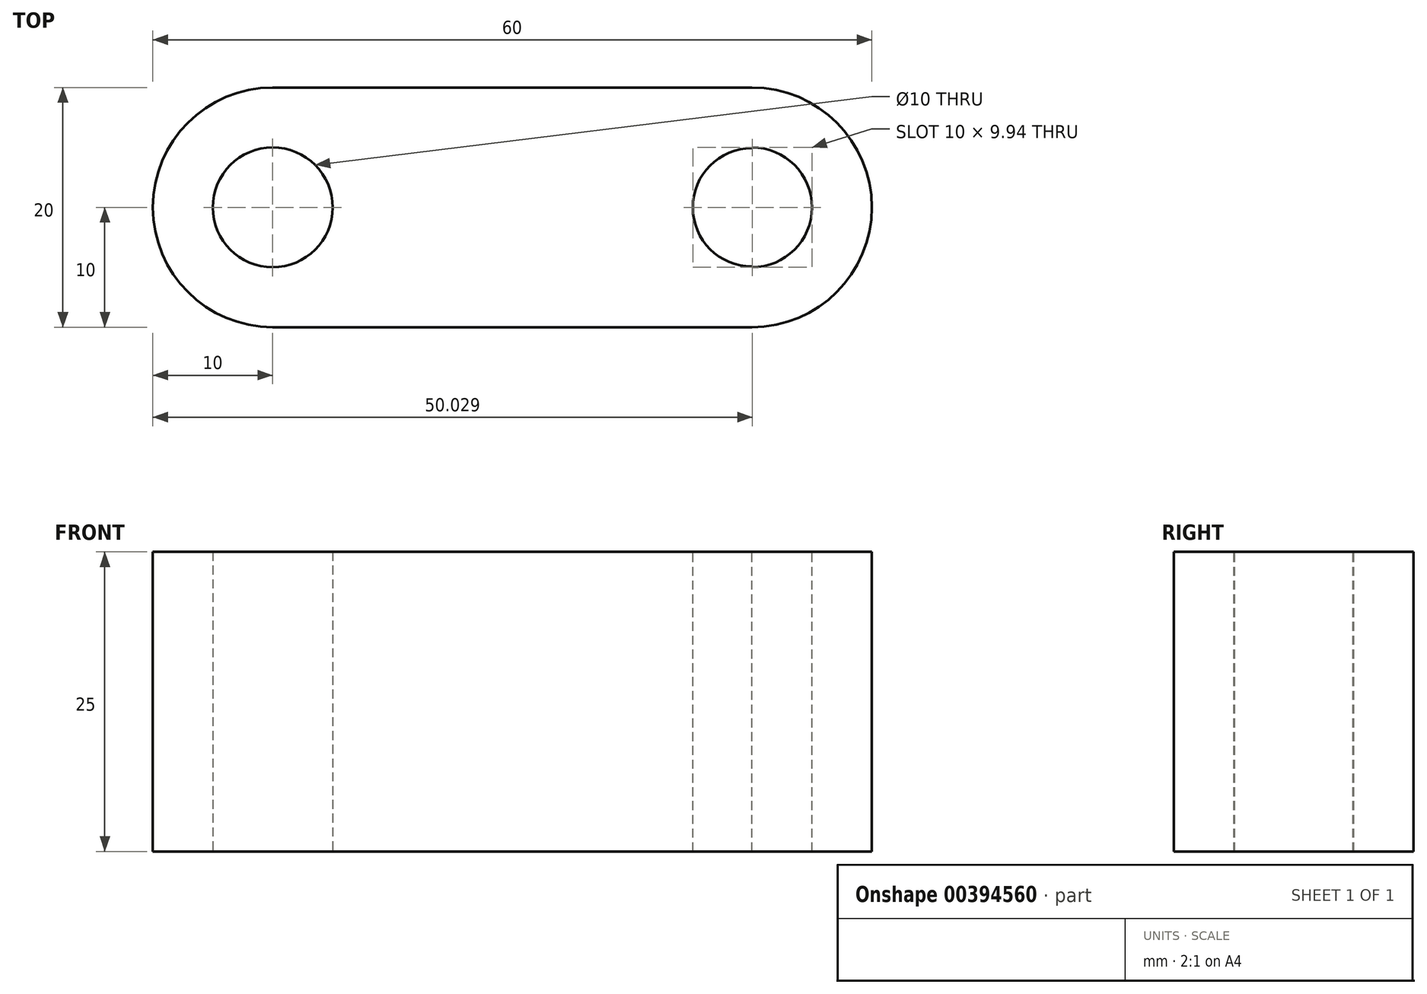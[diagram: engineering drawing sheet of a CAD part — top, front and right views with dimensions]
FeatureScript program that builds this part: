
annotation { "Feature Type Name" : "Feature", "Feature Type Description" : "" }
export const myFeature = defineFeature(function(context is Context, id is Id, definition is map)
    precondition{}
    {
        {
            var Q0;
            Q0=qCreatedBy(makeId("Top.planeOp"),FACE);
            var sketch = newSketch(context, id + "F0", { "sketchPlane" : qUnion([Q0])});
            skLineSegment(sketch, "E0.bottom", {"start": v(20, -10) * mm, "end": v(-20, -10) * mm});
            skLineSegment(sketch, "E0.top", {"start": v(20, 10) * mm, "end": v(-20, 10) * mm});
            skLineSegment(sketch, "E0.left", {"start": v(20, -10) * mm, "end": v(20, 10) * mm});
            skLineSegment(sketch, "E0.right", {"start": v(-20, -10) * mm, "end": v(-20, 10) * mm});
            skPoint(sketch, "E0.middle", {"position": v(0, 0) * mm});
            skCircle(sketch, "E1", {"center": v(-20, 0) * mm, "radius": 10 * mm});
            skCircle(sketch, "E2", {"center": v(-20, 0) * mm, "radius": 5 * mm});
            skSolve(sketch);
        }
        {
            var Q0;
            Q0 = qSketchRegion(id + "F0", true);
            extrude(context, id + "F1", {"entities" : qUnion([Q0]), "depth" : 25 * mm});
        }
        {
            var Q0;
            Q0=makeQuery(id+"F1.opExtrude","CAP_FACE",FACE,{"disambiguationData":[OSD([sQuery(id+"F0.wireOp",EDGE,"E0.bottom"),sQuery(id+"F0.wireOp",EDGE,"E0.top"),sQuery(id+"F0.wireOp",EDGE,"E0.left"),sQuery(id+"F0.wireOp",EDGE,"E1"),sQuery(id+"F0.wireOp",EDGE,"E2")])],"isStart":false});
            var sketch = newSketch(context, id + "F2", { "sketchPlane" : qUnion([Q0])});
            skCircle(sketch, "E3", {"center": v(20, 0) * mm, "radius": 10 * mm});
            skCircle(sketch, "E4", {"center": v(20, 0) * mm, "radius": 5 * mm});
            skSolve(sketch);
        }
        {
            var Q0;
            Q0 = qSketchRegion(id + "F2", true);
            extrude(context, id + "F3", {"entities" : qUnion([Q0]), "operationType" : NewBodyOperationType.ADD, "oppositeDirection" : true, "depth" : 25 * mm});
        }
        {
            var Q0;
            Q0=makeQuery(id+"F3.boolean.opBoolean","MERGE",FACE,{"derivedFrom":[makeQuery(id+"F1.opExtrude","CAP_FACE",FACE,{"disambiguationData":[OSD([sQuery(id+"F0.wireOp",EDGE,"E0.bottom"),sQuery(id+"F0.wireOp",EDGE,"E0.top"),sQuery(id+"F0.wireOp",EDGE,"E0.left"),sQuery(id+"F0.wireOp",EDGE,"E1"),sQuery(id+"F0.wireOp",EDGE,"E2")])],"isStart":false}),makeQuery(id+"F3.opExtrude","CAP_FACE",FACE,{"disambiguationData":[OSD([sQuery(id+"F2.wireOp",EDGE,"E3"),sQuery(id+"F2.wireOp",EDGE,"E4")])],"isStart":true})]});
            var sketch = newSketch(context, id + "F4", { "sketchPlane" : qUnion([Q0])});
            skCircle(sketch, "E5", {"center": v(20, 0) * mm, "radius": 4.94 * mm});
            skSolve(sketch);
        }
        {
            var Q0;
            Q0 = qSketchRegion(id + "F4", true);
            extrude(context, id + "F5", {"entities" : qUnion([Q0]), "operationType" : NewBodyOperationType.REMOVE, "endBound" : BoundingType.THROUGH_ALL, "oppositeDirection" : true, "depth" : 25 * mm});
        }
    });
